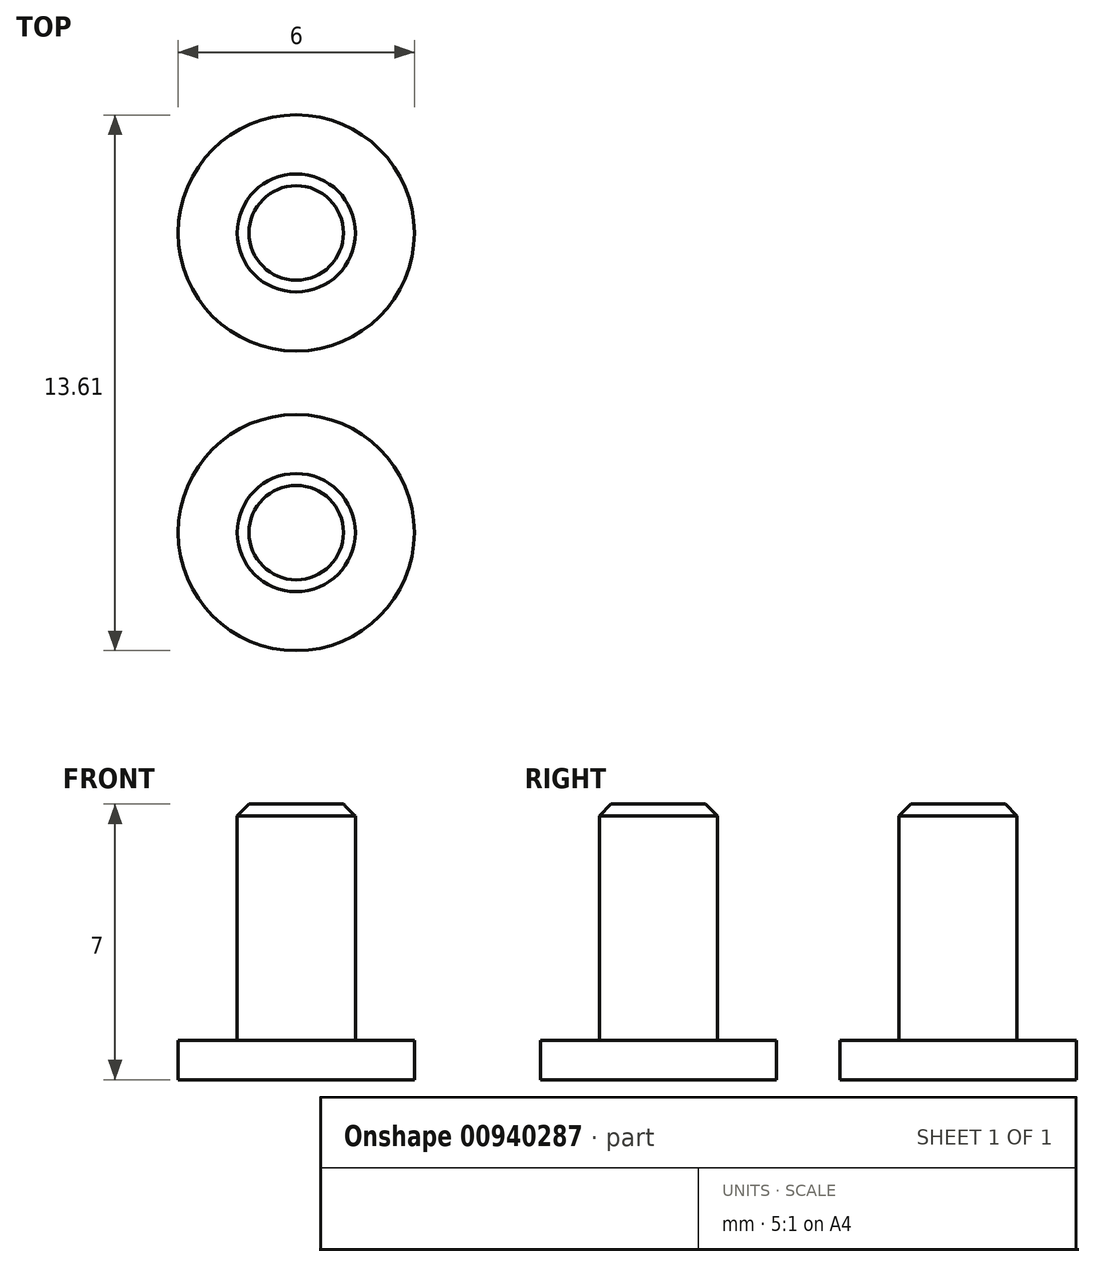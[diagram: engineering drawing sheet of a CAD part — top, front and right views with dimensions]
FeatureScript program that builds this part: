
annotation { "Feature Type Name" : "Feature", "Feature Type Description" : "" }
export const myFeature = defineFeature(function(context is Context, id is Id, definition is map)
    precondition{}
    {
        {
            var Q0;
            Q0=qCreatedBy(makeId("Top.planeOp"),FACE);
            var sketch = newSketch(context, id + "F0", { "sketchPlane" : qUnion([Q0])});
            skCircle(sketch, "E0", {"center": v(0, 0) * mm, "radius": 3 * mm});
            skCircle(sketch, "E1", {"center": v(0, 7.61) * mm, "radius": 3 * mm});
            skSolve(sketch);
        }
        {
            var Q0;
            Q0 = qSketchRegion(id + "F0", true);
            extrude(context, id + "F1", {"entities" : qUnion([Q0]), "depth" : 1 * mm, "offsetDistance" : 25 * mm});
        }
        {
            var Q0;
            Q0=makeQuery(id+"F1.opExtrude","CAP_FACE",FACE,{"disambiguationData":[OSD([sQuery(id+"F0.wireOp",EDGE,"E0")])],"isStart":false});
            var sketch = newSketch(context, id + "F2", { "sketchPlane" : qUnion([Q0])});
            skCircle(sketch, "E2", {"center": v(0, 0) * mm, "radius": 1.5 * mm});
            skCircle(sketch, "E3", {"center": v(0, 7.61) * mm, "radius": 1.5 * mm});
            skSolve(sketch);
        }
        {
            var Q0;
            Q0 = qSketchRegion(id + "F2", true);
            extrude(context, id + "F3", {"entities" : qUnion([Q0]), "operationType" : NewBodyOperationType.ADD, "depth" : 6 * mm, "offsetDistance" : 25 * mm});
        }
        {
            var Q0;
            Q0=makeQuery(id+"F3.opExtrude","CAP_EDGE",EDGE,{"disambiguationData":[OSD([sQuery(id+"F2.wireOp",EDGE,"E2")])],"isStart":false});
            var Q1;
            Q1=makeQuery(id+"F3.opExtrude","CAP_FACE",FACE,{"disambiguationData":[OSD([sQuery(id+"F2.wireOp",EDGE,"E3")])],"isStart":false});
            chamfer(context, id + "F4", {"entities" : qUnion([Q0, Q1]), "width" : 0.3 * mm, "tangentPropagation" : true});
        }
    });
